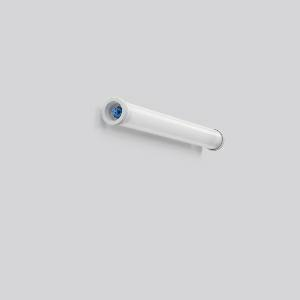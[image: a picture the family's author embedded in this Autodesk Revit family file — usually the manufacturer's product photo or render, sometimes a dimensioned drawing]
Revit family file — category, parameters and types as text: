
# Revit family: planox_tube_601070_002_730hf_3ccc
name_source: partatom
category: Lighting Fixtures
units: mm (PartAtom-declared; Revit-internal decimal feet)

## family parameters
Cut with Voids When Loaded = No
Host = Face
Light Source = No
Part Type = Normal
Room Calculation Point = No
Round Connector Dimension = Use Diameter
Shared = No

## types (1)
- PLANOX TUBE (1 x LED Modul 840, 3500 lm, 4000)
    Apparent Load = 31 VA
    CIE Flux Codes = 41 70 89 89 100
    Color Rendering = 80
    Color Temperature = 4000
    Default Elevation = 1800 mm
    Description = Series: PLANOX TUBE
Robust protective tube luminaire for tough requirements. Rack made of sheet steel, white powder coated. End caps made of plastic (polyamide) grey. Diffuser made of plastic (polycarbonate), opal, shockproof. Symmetrical light distribution. Homogeneous light distribution. With accessories for wall, ceiling or pendant mounting. Mounting set must be ordered separately. Luminaire with limited surface temperature in accordance with EN 60598-2-24 for use in environments in which a deposit of conductive dust on the luminaire can be expected. Qualified for use in the food and drink industry. Suitable for lighting in public car parks and public off-street parking spaces according to DIN 67528. Environmentally friendly and resource-saving due to replaceable components. 
Colour: white
Diameter: 78 mm
Length: 791 mm
Lamp: LED
Socket: without socket
Colour temperature: 4000K
Colour rendering index (CRI): 83
System power: 31 W
Rated luminous flux: 3500 lm
Luminous efficiency: 113 lm/W
Control gear: Dimmable Bluetooth converter
Protection class: I
Type of protection: IP 67
    Height = 0 mm  [stored 0 ft]
    Lamp = 1 x LED Modul 840
    Lamp Light Flux = 3500 lm
    Lamp count = 1
    Length = 791 mm
    Lifetime = 50000 h
    Luminous efficacy = 113 lm/W
    Manufacturer = RZB
    ModVariant = No
    Model = 601070.002.730HF
    Mounting Place = Ceiling, Wall
    Mounting Type = Surface mounted
    Number of Poles = 1
    OnlyDefault = Yes
    Power Factor = 1
    Product Name = PLANOX TUBE
    Product group = Surface mounted luminaires for moist/humid enviroments
    ProductGroupID = 308
    Protection Class = Protection class I
    Protection Degree = Degree of protection
    RLX_Detail_Level = 1
    RLX_Emergency_Light_Flux = 0 lm
    RLX_Emergency_Type = 0
    RLX_Emergency_Type_DB = No
    RlxData = <blob elided: 31521 chars, md5=d6757e42>
    Socket = socket
    Standby Power = 0 W
    System Light Flux = 3500 lm
    System Power = 31 W
    Type Comments = Product without accessories
    Type Image = 601070.002.jpg
    URL = http://relux.com
    VarID = ---
    Voltage = 230 V
    Voltage Range = 220-240 V
    Weight = 0.00 kg
    Width = 0 mm  [stored 0 ft]

note: [stored X ft] marks values corroborated as IEEE doubles in the binary element streams (Revit-internal decimal feet)

## geometry (parser evidence)
native form markers: Blend x4, Sweep x13
no freeform markers — native parametric forms only
